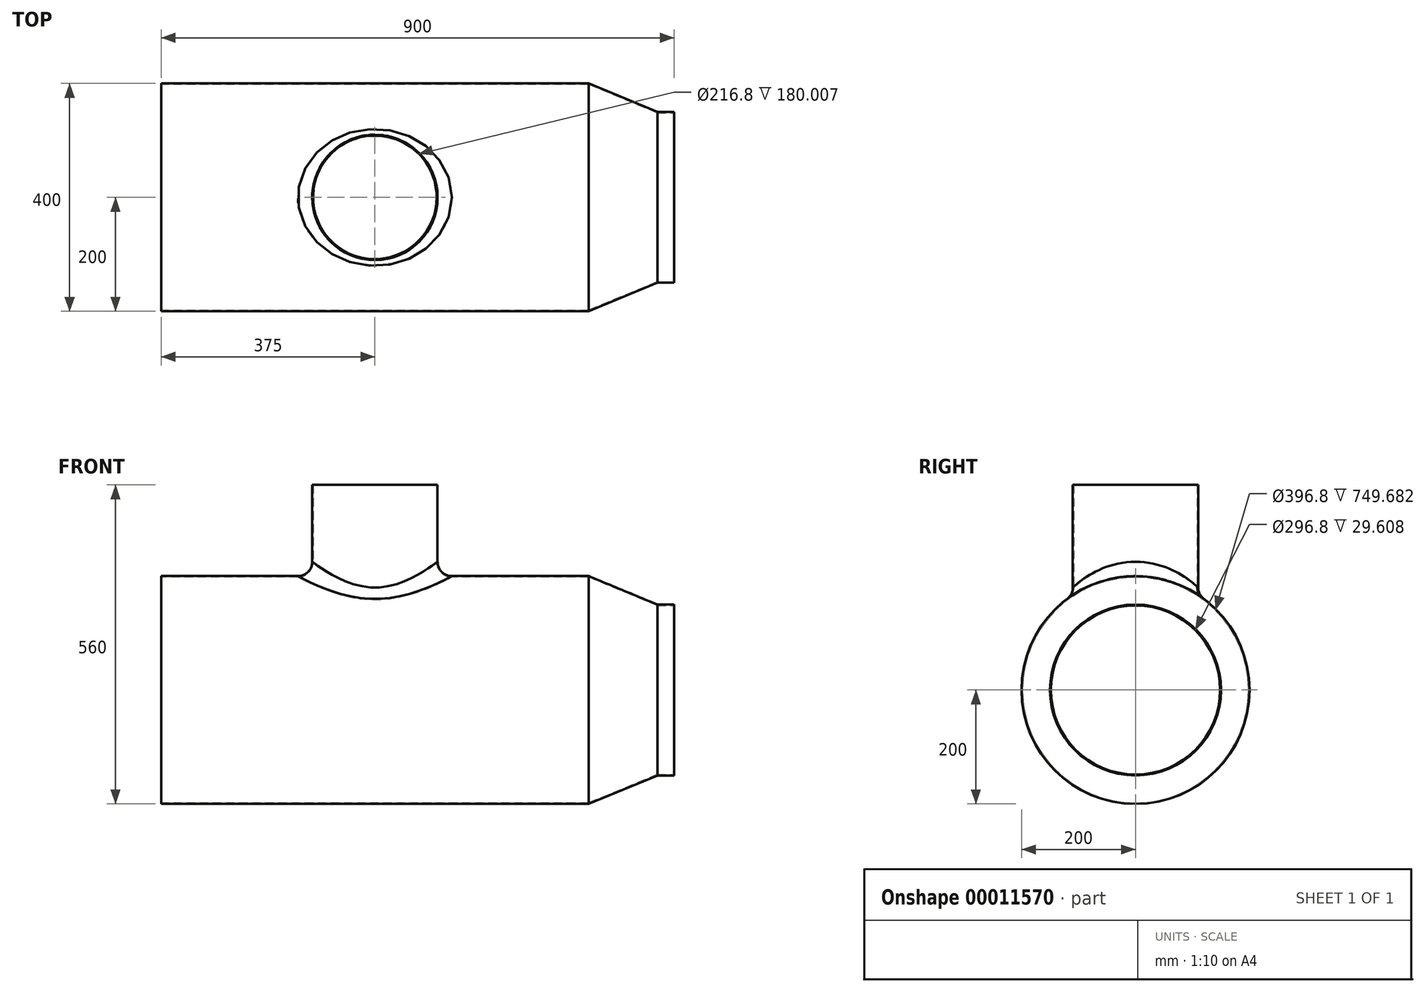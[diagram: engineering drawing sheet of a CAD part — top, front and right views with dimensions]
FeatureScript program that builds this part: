
annotation { "Feature Type Name" : "Feature", "Feature Type Description" : "" }
export const myFeature = defineFeature(function(context is Context, id is Id, definition is map)
    precondition{}
    {
        {
            var Q0;
            Q0=qCreatedBy(makeId("Right.planeOp"),FACE);
            var sketch = newSketch(context, id + "F0", { "sketchPlane" : qUnion([Q0])});
            skCircle(sketch, "E0", {"center": v(0, 0) * mm, "radius": 200 * mm});
            skSolve(sketch);
        }
        {
            var Q0;
            Q0=makeQuery(id+"F0.imprint","IMPRINT",FACE,{"disambiguationData":[TD([[makeQuery(id+"F0.imprint","IMPRINT",EDGE,{"derivedFrom":sQuery(id+"F0.wireOp",EDGE,"E0")}),1.0]])]});
            extrude(context, id + "F1", {"entities" : qUnion([Q0]), "endBound" : BoundingType.SYMMETRIC, "depth" : 750 * mm});
        }
        {
            var Q0;
            Q0=qCreatedBy(makeId("Top.planeOp"),FACE);
            var sketch = newSketch(context, id + "F2", { "sketchPlane" : qUnion([Q0])});
            skCircle(sketch, "E1", {"center": v(0, 0) * mm, "radius": 110 * mm});
            skSolve(sketch);
        }
        {
            var Q0;
            Q0 = qSketchRegion(id + "F2", true);
            extrude(context, id + "F3", {"entities" : qUnion([Q0]), "operationType" : NewBodyOperationType.ADD, "depth" : 360 * mm});
        }
        {
            var Q0;
            Q0=makeQuery(id+"F3.boolean.opBoolean","INTERSECT",EDGE,{"derivedFrom":[makeQuery(id+"F1.opExtrude","SWEPT_FACE",FACE,{"disambiguationData":[OSD([sQuery(id+"F0.wireOp",EDGE,"E0")])]}),makeQuery(id+"F3.opExtrude","SWEPT_FACE",FACE,{"disambiguationData":[OSD([sQuery(id+"F2.wireOp",EDGE,"E1")])]})]});
            fillet(context, id + "F4", {"entities" : qUnion([Q0]), "radius" : 25 * mm, "tangentPropagation" : true, "allowEdgeOverflow" : false});
        }
        {
            var Q0;
            Q0=makeQuery(id+"F1.opExtrude","CAP_FACE",FACE,{"disambiguationData":[OSD([sQuery(id+"F0.wireOp",EDGE,"E0")])],"isStart":false});
            var sketch = newSketch(context, id + "F5", { "sketchPlane" : qUnion([Q0])});
            skCircle(sketch, "E2", {"center": v(0, 0) * mm, "radius": 200 * mm});
            skSolve(sketch);
        }
        {
            var Q0;
            Q0 = qSketchRegion(id + "F5", true);
            extrude(context, id + "F6", {"entities" : qUnion([Q0]), "operationType" : NewBodyOperationType.ADD, "depth" : 150 * mm});
        }
        {
            var Q0;
            Q0=makeQuery(id+"F6.opExtrude","CAP_EDGE",EDGE,{"disambiguationData":[OSD([sQuery(id+"F5.wireOp",EDGE,"E2")])],"isStart":false});
            chamfer(context, id + "F7", {"entities" : qUnion([Q0]), "chamferType" : ChamferType.OFFSET_ANGLE, "width" : 150 * mm, "oppositeDirection" : true, "angle" : 22.5 * degree, "tangentPropagation" : true});
        }
        {
            var Q0;
            Q0=makeQuery(id+"F6.opExtrude","CAP_FACE",FACE,{"disambiguationData":[OSD([sQuery(id+"F5.wireOp",EDGE,"E2")])],"isStart":false});
            var sketch = newSketch(context, id + "F8", { "sketchPlane" : qUnion([Q0])});
            skCircle(sketch, "E3", {"center": v(0, 0) * mm, "radius": 150 * mm});
            skSolve(sketch);
        }
        {
            var Q0;
            Q0 = qSketchRegion(id + "F8", true);
            var Q1;
            Q1=makeQuery(id+"F7.opChamfer","BLEND_FACE",FACE,{"disambiguationData":[OSD([sQuery(id+"F5.wireOp",EDGE,"E2")])]});
            extrude(context, id + "F9", {"entities" : qUnion([Q0]), "operationType" : NewBodyOperationType.ADD, "endBound" : BoundingType.UP_TO_SURFACE, "oppositeDirection" : true, "endBoundEntityFace" : qUnion([Q1]), "depth" : 25 * mm});
        }
        {
            var Q0;
            Q0=makeQuery(id+"F1.opExtrude","CAP_FACE",FACE,{"disambiguationData":[OSD([sQuery(id+"F0.wireOp",EDGE,"E0")])],"isStart":true});
            var Q1;
            Q1=makeQuery(id+"F1.opExtrude","CAP_FACE",FACE,{"disambiguationData":[OSD([sQuery(id+"F0.wireOp",EDGE,"E0")])],"isStart":false});
            var Q2;
            Q2=makeQuery(id+"F3.opExtrude","CAP_FACE",FACE,{"disambiguationData":[OSD([sQuery(id+"F2.wireOp",EDGE,"E1")])],"isStart":false});
            var Q3;
            Q3=makeQuery(id+"F9.boolean.opBoolean","MERGE",FACE,{"derivedFrom":[makeQuery(id+"F6.opExtrude","CAP_FACE",FACE,{"disambiguationData":[OSD([sQuery(id+"F5.wireOp",EDGE,"E2")])],"isStart":false}),makeQuery(id+"F9.opExtrude","CAP_FACE",FACE,{"disambiguationData":[OSD([sQuery(id+"F8.wireOp",EDGE,"E3")])],"isStart":true})]});
            shell(context, id + "F10", {"entities" : qUnion([Q0, Q1, Q2, Q3]), "thickness" : 1.6 * mm});
        }
    });
